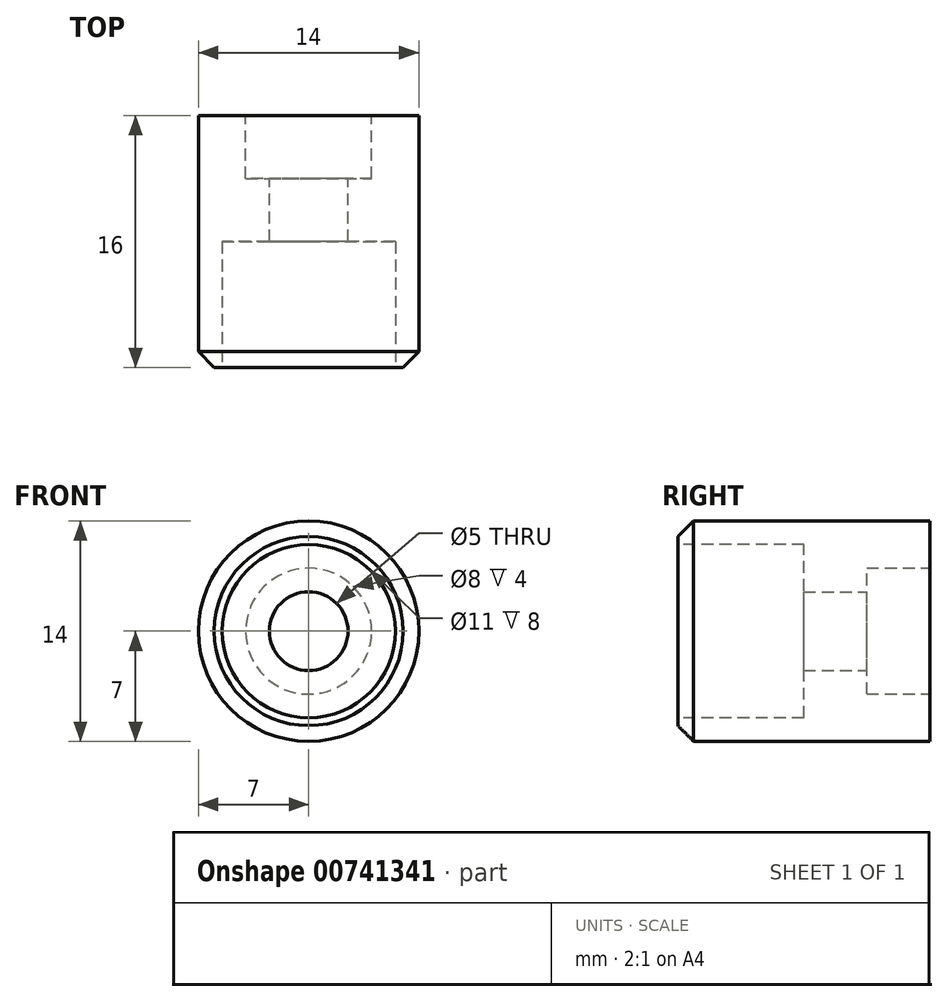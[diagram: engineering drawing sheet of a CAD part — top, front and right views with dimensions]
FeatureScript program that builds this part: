
annotation { "Feature Type Name" : "Feature", "Feature Type Description" : "" }
export const myFeature = defineFeature(function(context is Context, id is Id, definition is map)
    precondition{}
    {
        {
            var Q0;
            Q0=qCreatedBy(makeId("Front.planeOp"),FACE);
            var sketch = newSketch(context, id + "F0", { "sketchPlane" : qUnion([Q0])});
            skCircle(sketch, "E0", {"center": v(0, 0) * mm, "radius": 7 * mm});
            skCircle(sketch, "E1", {"center": v(0, 0) * mm, "radius": 2.5 * mm});
            skSolve(sketch);
        }
        {
            var Q0;
            Q0 = qSketchRegion(id + "F0", true);
            extrude(context, id + "F1", {"entities" : qUnion([Q0]), "depth" : 16 * mm, "offsetDistance" : 25 * mm});
        }
        {
            var Q0;
            Q0=qCreatedBy(makeId("Front.planeOp"),FACE);
            var sketch = newSketch(context, id + "F2", { "sketchPlane" : qUnion([Q0])});
            skCircle(sketch, "E2", {"center": v(0, 0) * mm, "radius": 4 * mm});
            skSolve(sketch);
        }
        {
            var Q0;
            Q0 = qSketchRegion(id + "F2", true);
            extrude(context, id + "F3", {"entities" : qUnion([Q0]), "operationType" : NewBodyOperationType.REMOVE, "depth" : 4 * mm, "offsetDistance" : 25 * mm});
        }
        {
            var Q0;
            Q0=makeQuery(id+"F1.opExtrude","CAP_EDGE",EDGE,{"disambiguationData":[OSD([sQuery(id+"F0.wireOp",EDGE,"E0")])],"isStart":false});
            chamfer(context, id + "F4", {"entities" : qUnion([Q0]), "width" : 1 * mm, "tangentPropagation" : true});
        }
        {
            var Q0;
            Q0=makeQuery(id+"F1.opExtrude","CAP_FACE",FACE,{"disambiguationData":[OSD([sQuery(id+"F0.wireOp",EDGE,"E0"),sQuery(id+"F0.wireOp",EDGE,"E1")])],"isStart":false});
            var sketch = newSketch(context, id + "F5", { "sketchPlane" : qUnion([Q0])});
            skCircle(sketch, "E3", {"center": v(0, 0) * mm, "radius": 5.5 * mm});
            skSolve(sketch);
        }
        {
            var Q0;
            Q0=makeQuery(id+"F2.imprint","IMPRINT",FACE,{"disambiguationData":[TD([[makeQuery(id+"F2.imprint","IMPRINT",EDGE,{"derivedFrom":sQuery(id+"F2.wireOp",EDGE,"E2")}),1.0]])]});
            var Q1;
            Q1 = qSketchRegion(id + "F5", true);
            extrude(context, id + "F6", {"entities" : qUnion([Q0, Q1]), "operationType" : NewBodyOperationType.REMOVE, "oppositeDirection" : true, "depth" : 8 * mm, "offsetDistance" : 25 * mm});
        }
    });
